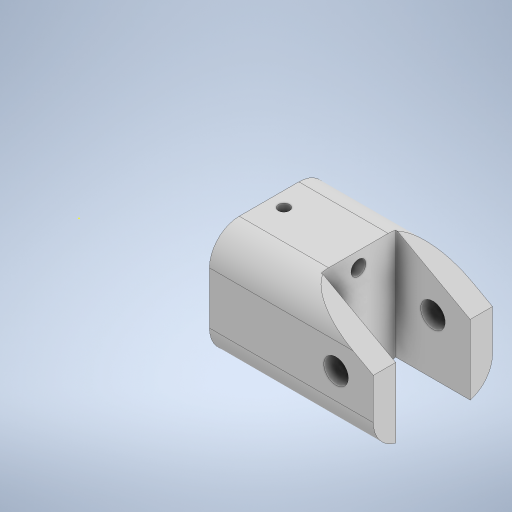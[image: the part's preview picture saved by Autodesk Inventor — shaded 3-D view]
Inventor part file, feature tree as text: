
AUTODESK INVENTOR PART (.ipt)
format: ipt  version: 2024 (Build 280153020, 153B)  size: 407,552 bytes
history: native  units: mm
features: sketch x18, extrude x15, chamfer x3, plane x1, split x1, move_body x1, delete_face x1, fillet x1
ambient origin geometry x8: Origin, YZ Plane, XZ Plane, XY Plane, X Axis, Y Axis, Z Axis, Center Point
bodies: Solid1 (feature_tree), Solid2 (feature_tree), Solid3 (feature_tree)
feature tree (41):
  extrude  "Extrusion1"  Depth=16.0mm
  sketch  "Sketch2"  dims[d2=15.0mm d3=0.0mm d4=10.0mm]
  extrude  "Extrusion2"  Depth=10.0mm
  chamfer  "Chamfer1"  Distance=21.25mm
  extrude  "Extrusion3"  Depth=10.0mm TaperAngle=0.0deg
  extrude  "Extrusion4"  Depth=11.5mm TaperAngle=0.0deg
  extrude  "Extrusion5"  Depth=1.0mm TaperAngle=0.0deg
  chamfer  "Chamfer2"  Distance=6.0mm Angle=45.0deg
  sketch  "Sketch6"  dims[d14=7.0mm d15=11.5mm d16=0.0mm]
  extrude  "Extrusion6"  Depth=9.0mm
  extrude  "Extrusion7"  Depth=45.25mm TaperAngle=0.0deg
  chamfer  "Chamfer3"  Distance=11.5mm Angle=45.0deg
  sketch  "Sketch9"  dims[d26=3.3mm d27=45.25mm d28=0.0mm d29=11.5mm d30=5.5mm d31=45.0deg]
  extrude  "Extrusion8"  Depth=65.75mm TaperAngle=0.0deg
  extrude  "Extrusion9"  Depth=9.0mm TaperAngle=0.0deg
  extrude  "Extrusion10"  Depth=13.0mm TaperAngle=0.0deg
  sketch  "Sketch13"  dims[d43=24.0mm d44=21.0mm d45=0.0mm]
  extrude  "Extrusion11"  Depth=21.0mm TaperAngle=0.0deg
  extrude  "Extrusion12"  TaperAngle=0.0deg  [1 undecoded]
  extrude  "Extrusion13"  Depth=4.0mm
  plane  "Work Plane1"
  split  "Split1"
  move_body  "Move Body1"
  extrude  "Extrusion14"  Depth=1.5mm
  delete_face  "Delete Face1"
  fillet  "Fillet1"  Radius=2.0mm
  extrude  "Extrusion15"  [1 undecoded]
  sketch  "Sketch1"  dims[d0=36.0mm d1=16.0mm]
  sketch  "Sketch3"  dims[d5=10.0mm]
  sketch  "Sketch4"  dims[d6=3.3mm d7=21.25mm d8=0.0mm]
  sketch  "Sketch5"  dims[d9=10.0mm d10=5.5mm d11=45.0deg d12=10.0mm d13=0.0mm]
  sketch  "Sketch7"  dims[d17=3.3mm d18=1.0mm d19=0.0mm d20=6.0mm d21=11.5mm d22=45.0deg]
  sketch  "Sketch8"  dims[d23=15.0mm d24=0.0mm d25=9.0mm]
  sketch  "Sketch10"  dims[d32=2.0mm d33=65.75mm d34=0.0mm]
  sketch  "Sketch11"  dims[d35=0.5mm d36=0.0mm d37=9.0mm d38=0.0mm]
  sketch  "Sketch12"  dims[d39=0.5mm d40=0.0mm d41=13.0mm d42=0.0mm]
  sketch  "Sketch14"  dims[d46=12.25mm d47=-12.0mm d48=0.0mm d49=0.0mm]
  sketch  "Sketch15"  dims[d50=10.0mm d51=0.0mm d52=4.0mm]
  sketch  "Sketch16"  dims[d53=2.0mm d54=1.5mm d55=2.0mm d56=0.0mm]
  sketch  "Sketch17"
  sketch  "Sketch18"
note: 2 required parameter values undecoded (feature->parameter linkage not recoverable at this tier; creation-order binding heuristic only, values carry confidence <= 0.55)
